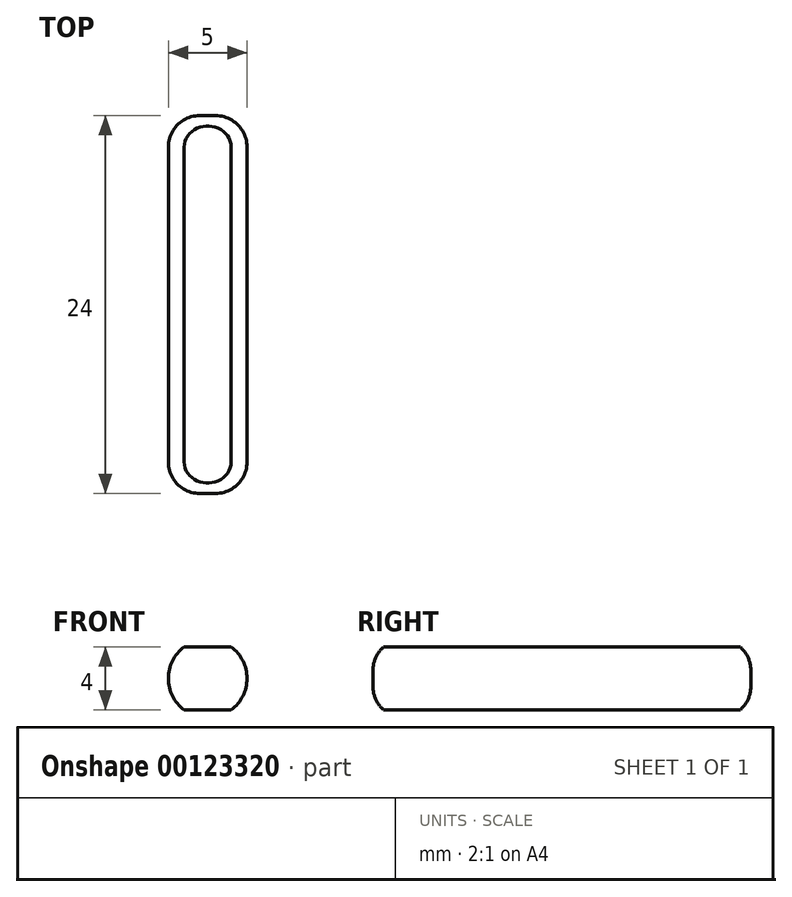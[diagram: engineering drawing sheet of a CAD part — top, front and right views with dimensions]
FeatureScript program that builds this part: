
annotation { "Feature Type Name" : "Feature", "Feature Type Description" : "" }
export const myFeature = defineFeature(function(context is Context, id is Id, definition is map)
    precondition{}
    {
        {
            var Q0;
            Q0=qCreatedBy(makeId("Front.planeOp"),FACE);
            var sketch = newSketch(context, id + "F0", { "sketchPlane" : qUnion([Q0])});
            skCircle(sketch, "E0", {"center": v(0, 0) * mm, "radius": 2.5 * mm, "construction": true});
            skLineSegment(sketch, "E1", {"start": v(-1.5, 2) * mm, "end": v(1.5, 2) * mm});
            skLineSegment(sketch, "E2", {"start": v(-1.5, -2) * mm, "end": v(1.5, -2) * mm});
            skArc(sketch, "E3", {"start": v(-1.5, 2) * mm, "mid": v(-2.5, 0) * mm, "end": v(-1.5, -2) * mm});
            skArc(sketch, "E4", {"start": v(1.5, -2) * mm, "mid": v(2.5, 0) * mm, "end": v(1.5, 2) * mm});
            skSolve(sketch);
        }
        {
            var Q0;
            Q0 = qSketchRegion(id + "F0", true);
            extrude(context, id + "F1", {"entities" : qUnion([Q0]), "depth" : 24 * mm});
        }
        {
            var Q0;
            Q0=makeQuery(id+"F1.opExtrude","CAP_EDGE",EDGE,{"disambiguationData":[OSD([sQuery(id+"F0.wireOp",EDGE,"E3")])],"isStart":false});
            var Q1;
            Q1=makeQuery(id+"F1.opExtrude","CAP_EDGE",EDGE,{"disambiguationData":[OSD([sQuery(id+"F0.wireOp",EDGE,"E4")])],"isStart":true});
            fillet(context, id + "F2", {"entities" : qUnion([Q0, Q1]), "radius" : 2 * mm, "tangentPropagation" : true, "allowEdgeOverflow" : false});
        }
    });
